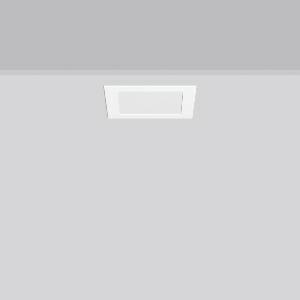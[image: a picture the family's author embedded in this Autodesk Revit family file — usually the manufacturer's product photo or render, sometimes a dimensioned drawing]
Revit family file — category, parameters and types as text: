
# Revit family: toledo_flat_square_e_672242_002_1_89_a642
name_source: partatom
category: Lighting Fixtures
units: mm (PartAtom-declared; Revit-internal decimal feet)

## family parameters
Cut with Voids When Loaded = No
Host = Face
Light Source = No
Part Type = Normal
Room Calculation Point = No
Round Connector Dimension = Use Diameter
Shared = No

## types (1)
- TOLEDO FLAT square E (1 x LED Modul 840, 750 lm, 4000)
    Apparent Load = 9 VA
    CIE Flux Codes = 49 80 96 100 100
    Color Rendering = 80
    Color Temperature = 4000
    Default Elevation = 1800 mm
    Description = Series: TOLEDO FLAT square
Square recessed downlight. For escape route illumination. Housing: die-cast aluminium, powder-coated. Lightguide and diffuser made of non-yellowing plastic (PMMA). Diffuser opal matt plastic. Ceiling installation with spring system. Including separate LED converter with connecting cable 250 mm. Suitable for connection to central battery systems. With AC Control monitoring module for LUXIFAIR central battery units. External driver with simple plug-in locking system. 
Colour: white
Length: 172 mm
Width: 172 mm
Height: 3 mm
Cut-out length: 156 mm
Cut-out width: 156 mm
Recess height: 60 mm
Luminaire: recess height: 37-57 mm
Weight: 1.21 kg
Operating mode: maintained power mode
Lamp: LED
Socket: without socket
Colour temperature: 4000K
Colour rendering index (CRI): 80
System power: 9 W
Rated luminous flux: 750 lm
Luminous flux, emergency: 750 lm
System power, emergency: 9 W
Control gear: Regulated power supply
Protection class: I
Type of protection: IP 54
    Height = 0 mm  [stored 0 ft]
    Lamp = 1 x LED Modul 840
    Lamp Light Flux = 750 lm
    Lamp count = 1
    Length = 172 mm
    Lifetime = 50000 h
    Luminous efficacy = 83 lm/W
    Manufacturer = RZB
    ModVariant = No
    Model = 672242.002.1.89
    Mounting Place = Ceiling
    Mounting Type = Recessed
    Number of Poles = 1
    OnlyDefault = Yes
    Power Factor = 1
    Product Name = TOLEDO FLAT square E
    Product group = Recessed downlights
    ProductGroupID = 402
    Protection Class = Protection class I
    Protection Degree = IP 40
    RLX_Detail_Level = 1
    RLX_Emergency_Light_Flux = 750 lm
    RLX_Emergency_Type = 3
    RLX_Emergency_Type_DB = Yes
    RlxData = <blob elided: 10089 chars, md5=b1fd339a>
    Socket = socket
    Standby Power = 0 W
    System Light Flux = 750 lm
    System Power = 9 W
    Type Comments = Product without accessories
    Type Image = 901486.002.jpg
    URL = http://relux.com
    VarID = ---
    Voltage = 230 V
    Voltage Range = 220-240 V
    Weight = 0.00 kg
    Width = 172 mm

note: [stored X ft] marks values corroborated as IEEE doubles in the binary element streams (Revit-internal decimal feet)

## geometry (parser evidence)
native form markers: Sweep x9
no freeform markers — native parametric forms only
